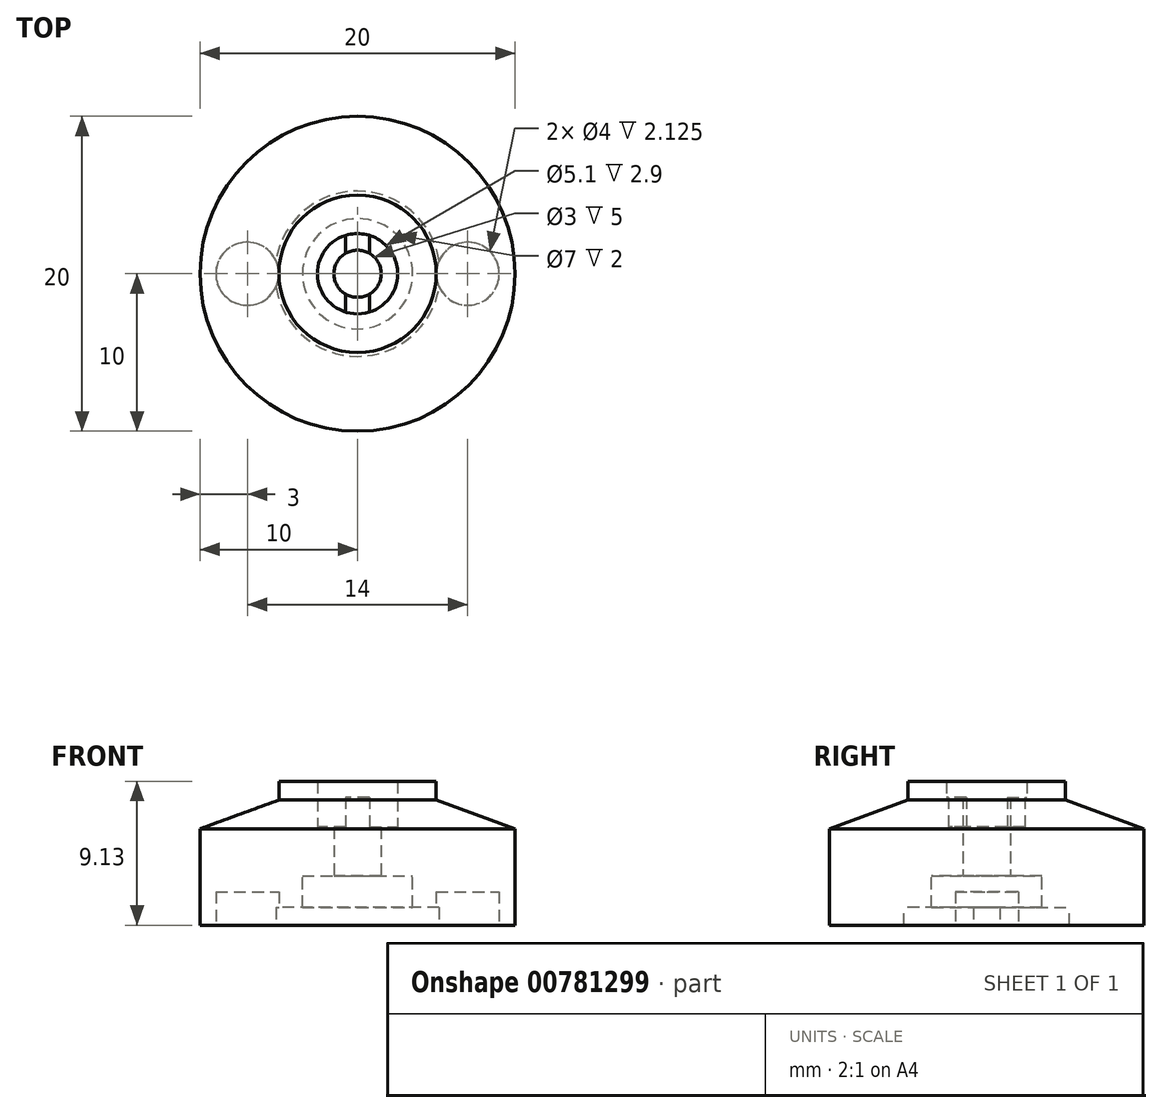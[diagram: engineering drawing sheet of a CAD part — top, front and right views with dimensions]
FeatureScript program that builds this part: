
annotation { "Feature Type Name" : "Feature", "Feature Type Description" : "" }
export const myFeature = defineFeature(function(context is Context, id is Id, definition is map)
    precondition{}
    {
        {
            var Q0;
            Q0=qCreatedBy(makeId("Top.planeOp"),FACE);
            var sketch = newSketch(context, id + "F0", { "sketchPlane" : qUnion([Q0])});
            skCircle(sketch, "E0", {"center": v(0, 0) * mm, "radius": 2.55 * mm});
            skCircle(sketch, "E1", {"center": v(0, 0) * mm, "radius": 5 * mm});
            skCircle(sketch, "E2", {"center": v(0, 0) * mm, "radius": 1.5 * mm});
            skLineSegment(sketch, "E3", {"start": v(-0.75, 1.3) * mm, "end": v(-0.75, 2.44) * mm});
            skLineSegment(sketch, "E4", {"start": v(0.75, 1.3) * mm, "end": v(0.75, 2.44) * mm});
            skLineSegment(sketch, "E5", {"start": v(-0.75, -1.3) * mm, "end": v(-0.75, -2.44) * mm});
            skLineSegment(sketch, "E6", {"start": v(0.75, -1.3) * mm, "end": v(0.75, -2.44) * mm});
            skSolve(sketch);
        }
        {
            var Q0;
            Q0=makeQuery(id+"F0.imprint","IMPRINT",FACE,{"disambiguationData":[TD([[makeQuery(id+"F0.imprint","IMPRINT",EDGE,{"derivedFrom":sQuery(id+"F0.wireOp",EDGE,"E1")}),1.0]])]});
            extrude(context, id + "F1", {"entities" : qUnion([Q0]), "depth" : 6 * mm, "offsetDistance" : 25 * mm});
        }
        {
            var Q0;
            {var subQ0=sQuery(id+"F0.wireOp",EDGE,"E3");Q0=makeQuery(id+"F0.imprint","IMPRINT",FACE,{"disambiguationData":[TD([[makeQuery(id+"F0.imprint","IMPRINT",EDGE,{"derivedFrom":subQ0}),-1.0]])]});}
            var Q1;
            {var subQ0=sQuery(id+"F0.wireOp",EDGE,"E5");Q1=makeQuery(id+"F0.imprint","IMPRINT",FACE,{"disambiguationData":[TD([[makeQuery(id+"F0.imprint","IMPRINT",EDGE,{"derivedFrom":subQ0}),1.0]])]});}
            extrude(context, id + "F2", {"entities" : qUnion([Q0, Q1]), "operationType" : NewBodyOperationType.ADD, "depth" : 5 * mm, "offsetDistance" : 25 * mm});
        }
        {
            var Q0;
            {var subQ0=sQuery(id+"F0.wireOp",EDGE,"E3");Q0=makeQuery(id+"F0.imprint","IMPRINT",FACE,{"disambiguationData":[TD([[makeQuery(id+"F0.imprint","IMPRINT",EDGE,{"derivedFrom":subQ0}),1.0]])]});}
            var Q1;
            {var subQ0=sQuery(id+"F0.wireOp",EDGE,"E4");Q1=makeQuery(id+"F0.imprint","IMPRINT",FACE,{"disambiguationData":[TD([[makeQuery(id+"F0.imprint","IMPRINT",EDGE,{"derivedFrom":subQ0}),-1.0]])]});}
            extrude(context, id + "F3", {"entities" : qUnion([Q0, Q1]), "operationType" : NewBodyOperationType.ADD, "depth" : 3.1 * mm, "offsetDistance" : 25 * mm});
        }
        {
            var Q0;
            Q0=qCreatedBy(makeId("Front.planeOp"),FACE);
            var sketch = newSketch(context, id + "F4", { "sketchPlane" : qUnion([Q0])});
            skLineSegment(sketch, "E7", {"start": v(0, 0) * mm, "end": v(-10, 0) * mm});
            skLineSegment(sketch, "E8", {"start": v(-10, 0) * mm, "end": v(-10, 3) * mm});
            skLineSegment(sketch, "E9", {"start": v(-10, 3) * mm, "end": v(-4.5, 5) * mm});
            skLineSegment(sketch, "E10", {"start": v(-4.5, 5) * mm, "end": v(-4, 5) * mm});
            skLineSegment(sketch, "E11", {"start": v(-4, 5) * mm, "end": v(-4, 0) * mm});
            skLineSegment(sketch, "E12", {"start": v(0, -1.5) * mm, "end": v(0, 4) * mm, "construction": true});
            skSolve(sketch);
        }
        {
            var Q0;
            Q0 = qSketchRegion(id + "F4", true);
            var Q1;
            Q1=sQuery(id+"F4.wireOp",EDGE,"E12");
            revolve(context, id + "F5", {"operationType" : NewBodyOperationType.ADD, "surfaceOperationType" : NewSurfaceOperationType.NEW, "entities" : qUnion([Q0]), "axis" : qUnion([Q1]), "revolveType" : RevolveType.FULL});
        }
        {
            var Q0;
            {var subQ0=sQuery(id+"F0.wireOp",EDGE,"E6");var subQ1=sQuery(id+"F0.wireOp",EDGE,"E4");var subQ2=sQuery(id+"F0.wireOp",EDGE,"E2");var subQ3=sQuery(id+"F0.wireOp",EDGE,"E0");var subQ4=sQuery(id+"F0.wireOp",EDGE,"E5");var subQ5=sQuery(id+"F0.wireOp",EDGE,"E3");Q0=makeQuery(id+"F5.boolean.opBoolean","MERGE",FACE,{"derivedFrom":[makeQuery(id+"F3.boolean.opBoolean","MERGE",FACE,{"derivedFrom":[makeQuery(id+"F2.boolean.opBoolean","MERGE",FACE,{"derivedFrom":[makeQuery(id+"F1.opExtrude","CAP_FACE",FACE,{"disambiguationData":[OSD([subQ3,sQuery(id+"F0.wireOp",EDGE,"E1")])],"isStart":true}),makeQuery(id+"F2.opExtrude","CAP_FACE",FACE,{"disambiguationData":[OSD([subQ3,subQ2,subQ5,subQ1])],"isStart":true}),makeQuery(id+"F2.opExtrude","CAP_FACE",FACE,{"disambiguationData":[OSD([subQ3,subQ2,subQ4,subQ0])],"isStart":true})]}),makeQuery(id+"F3.opExtrude","CAP_FACE",FACE,{"disambiguationData":[OSD([subQ3,subQ2,subQ5,subQ4])],"isStart":true}),makeQuery(id+"F3.opExtrude","CAP_FACE",FACE,{"disambiguationData":[OSD([subQ3,subQ2,subQ1,subQ0])],"isStart":true})]}),makeQuery(id+"F5.opRevolve","SWEPT_FACE",FACE,{"disambiguationData":[OSD([sQuery(id+"F4.wireOp",EDGE,"E7")])]})]});}
            var sketch = newSketch(context, id + "F6", { "sketchPlane" : qUnion([Q0])});
            skCircle(sketch, "E13", {"center": v(0, 0) * mm, "radius": 3.5 * mm});
            skSolve(sketch);
        }
        {
            var Q0;
            Q0=makeQuery(id+"F6.imprint","IMPRINT",FACE,{"disambiguationData":[TD([[makeQuery(id+"F6.imprint","IMPRINT",EDGE,{"derivedFrom":sQuery(id+"F6.wireOp",EDGE,"E13")}),-1.0]])]});
            extrude(context, id + "F7", {"entities" : qUnion([Q0]), "operationType" : NewBodyOperationType.ADD, "depth" : 2 * mm, "offsetDistance" : 25 * mm});
        }
        {
            var Q0;
            Q0=makeQuery(id+"F7.opExtrude","CAP_FACE",FACE,{"disambiguationData":[OSD([sQuery(id+"F4.wireOp",EDGE,"E7"),sQuery(id+"F4.wireOp",EDGE,"E8"),sQuery(id+"F6.wireOp",EDGE,"E13")])],"isStart":false});
            var sketch = newSketch(context, id + "F8", { "sketchPlane" : qUnion([Q0])});
            skCircle(sketch, "E14", {"center": v(0, 0) * mm, "radius": 5.25 * mm});
            skSolve(sketch);
        }
        {
            var Q0;
            Q0=makeQuery(id+"F8.imprint","IMPRINT",FACE,{"disambiguationData":[TD([[makeQuery(id+"F8.imprint","IMPRINT",EDGE,{"derivedFrom":sQuery(id+"F8.wireOp",EDGE,"E14")}),-1.0]])]});
            extrude(context, id + "F9", {"entities" : qUnion([Q0]), "operationType" : NewBodyOperationType.ADD, "depth" : 1.12 * mm, "offsetDistance" : 25 * mm});
        }
        {
            var Q0;
            Q0=makeQuery(id+"F9.opExtrude","CAP_FACE",FACE,{"disambiguationData":[OSD([sQuery(id+"F4.wireOp",EDGE,"E7"),sQuery(id+"F4.wireOp",EDGE,"E8"),sQuery(id+"F8.wireOp",EDGE,"E14")])],"isStart":false});
            var sketch = newSketch(context, id + "F10", { "sketchPlane" : qUnion([Q0])});
            skPoint(sketch, "E15", {"position": v(-7, 0) * mm});
            skPoint(sketch, "E16", {"position": v(7, 0) * mm});
            skLineSegment(sketch, "E17", {"start": v(-7, 2) * mm, "end": v(-4.85, 2) * mm});
            skLineSegment(sketch, "E18", {"start": v(-7, -2) * mm, "end": v(-4.85, -2) * mm});
            skLineSegment(sketch, "E19", {"start": v(7, -2) * mm, "end": v(4.85, -2) * mm});
            skLineSegment(sketch, "E20", {"start": v(7, 2) * mm, "end": v(4.85, 2) * mm});
            skCircle(sketch, "E21", {"center": v(-7, 0) * mm, "radius": 2 * mm});
            skCircle(sketch, "E22", {"center": v(7, 0) * mm, "radius": 2 * mm});
            skSolve(sketch);
        }
        {
            var Q0;
            Q0 = qSketchRegion(id + "F10", true);
            extrude(context, id + "F11", {"entities" : qUnion([Q0]), "operationType" : NewBodyOperationType.REMOVE, "oppositeDirection" : true, "depth" : 2.12 * mm, "offsetDistance" : 25 * mm});
        }
    });
